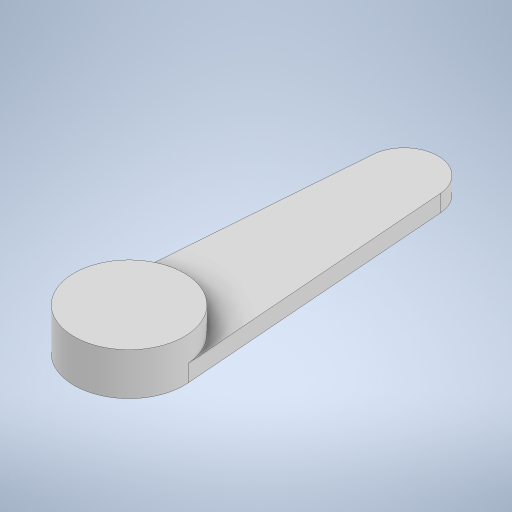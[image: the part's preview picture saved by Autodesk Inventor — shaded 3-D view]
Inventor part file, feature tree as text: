
AUTODESK INVENTOR PART (.ipt)
format: ipt  version: 2024 (Build 280153000, 153)  size: 226,816 bytes
history: native  units: in
note: dims shown in document units (in); Inventor stores cm internally (conversion verified against a paired STEP export)
features: extrude x2, sketch x1
ambient origin geometry x8: Origin, YZ Plane, XZ Plane, XY Plane, X Axis, Y Axis, Z Axis, Center Point
bodies: Solid1 (feature_tree)
feature tree (3):
  sketch  "Sketch1"  dims[d0=0.2559in d1=0.1575in d2=0.8465in d3=0.0394in d4=0.0in d5=0.0984in d6=0.0in]
  extrude  "Extrusion1"  Depth=0.0984in
  extrude  "Extrusion2"  Depth=0.0984in
